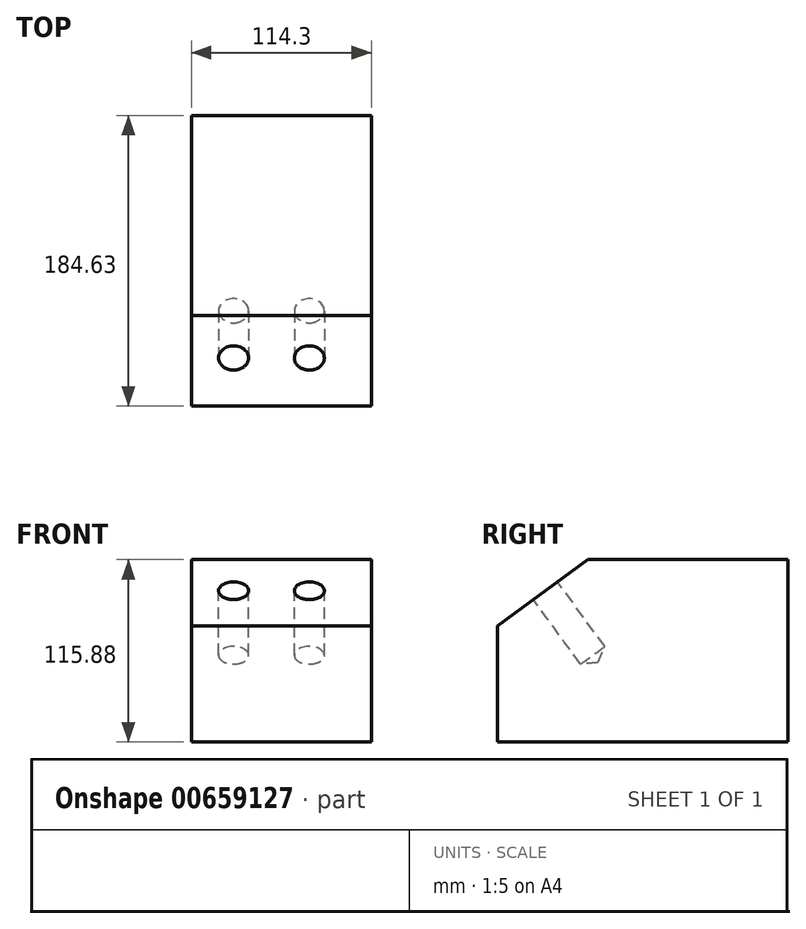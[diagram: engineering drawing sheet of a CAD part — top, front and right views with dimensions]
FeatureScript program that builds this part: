
annotation { "Feature Type Name" : "Feature", "Feature Type Description" : "" }
export const myFeature = defineFeature(function(context is Context, id is Id, definition is map)
    precondition{}
    {
        {
            var Q0;
            Q0=qCreatedBy(makeId("Right.planeOp"),FACE);
            var sketch = newSketch(context, id + "F0", { "sketchPlane" : qUnion([Q0])});
            skLineSegment(sketch, "E0", {"start": v(0, 0) * mm, "end": v(127, 0) * mm});
            skLineSegment(sketch, "E1", {"start": v(0, 0) * mm, "end": v(-57.63, -42.12) * mm});
            skLineSegment(sketch, "E2", {"start": v(-57.63, -42.12) * mm, "end": v(-57.63, -115.88) * mm});
            skLineSegment(sketch, "E3", {"start": v(-57.63, -115.88) * mm, "end": v(127, -115.88) * mm});
            skLineSegment(sketch, "E4", {"start": v(127, -115.88) * mm, "end": v(127, 0) * mm});
            skSolve(sketch);
        }
        {
            var Q0;
            Q0=makeQuery(id+"F0.imprint","IMPRINT",FACE,{"disambiguationData":[TD([[makeQuery(id+"F0.imprint","IMPRINT",EDGE,{"derivedFrom":sQuery(id+"F0.wireOp",EDGE,"E0")}),-1.0]])]});
            extrude(context, id + "F1", {"entities" : qUnion([Q0]), "depth" : 114.3 * mm, "offsetDistance" : 25.4 * mm});
        }
        {
            var Q0;
            Q0=makeQuery(id+"F1.opExtrude","SWEPT_FACE",FACE,{"disambiguationData":[OSD([sQuery(id+"F0.wireOp",EDGE,"E1")])]});
            var sketch = newSketch(context, id + "F2", { "sketchPlane" : qUnion([Q0])});
            skPoint(sketch, "E5", {"position": v(74.9, -33.5) * mm});
            skPoint(sketch, "E6", {"position": v(26.81, -33.5) * mm});
            skSolve(sketch);
        }
        {
            var Q0;
            Q0=sQuery(id+"F2.wireOp",VERTEX,"E5");
            var Q1;
            Q1=sQuery(id+"F2.wireOp",VERTEX,"E6");
            var Q2;
            Q2=makeQuery(id+"F1.opExtrude","SWEPT_BODY",BODY,{"disambiguationData":[OSD([sQuery(id+"F0.wireOp",EDGE,"E0"),sQuery(id+"F0.wireOp",EDGE,"E1"),sQuery(id+"F0.wireOp",EDGE,"E2"),sQuery(id+"F0.wireOp",EDGE,"E3"),sQuery(id+"F0.wireOp",EDGE,"E4")])]});
            hole(context, id + "F3", {"style" : HoleStyle.SIMPLE, "endStyle" : HoleEndStyle.BLIND, "holeDiameter" : 19.05 * mm, "majorDiameter" : 6.35 * mm, "holeDepth" : 50.8 * mm, "isTappedThrough" : true, "tappedDepth" : 12.7 * mm, "tapClearance" : 3, "locations" : qUnion([Q0, Q1]), "scope" : qUnion([Q2])});
        }
    });
